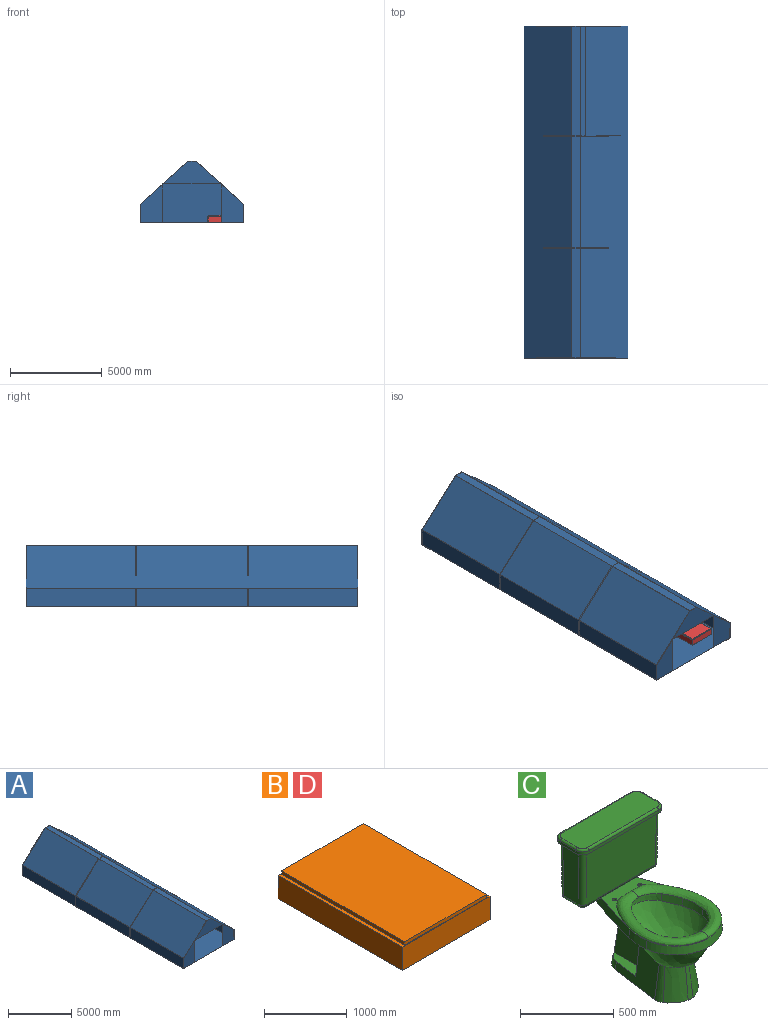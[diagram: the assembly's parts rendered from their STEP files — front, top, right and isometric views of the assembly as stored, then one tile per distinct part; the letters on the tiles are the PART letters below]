
ASSEMBLY  parts=4 mates=3
PART A: 45 faces, bbox 5640x18040x3323 mm
  f0: plane 5938.33x2228.5mm, normal (-0.67,0,-0.74), area 17807532.8mm2, adj f14,f26,f30,f36
  f1: plane 5963.33x2228.5mm, normal (0,0,1), area 13258575.8mm2, adj f14,f24,f26,f27,f30,f36
  f2: plane 3321.5x3313mm, normal (0,1,0), area 7985728.2mm2, adj f11,f12,f13,f15,f16,f35
  f3: plane 2093x25mm, normal (0,0,-1), area 52325mm2, adj f4,f24,f29,f35
  f4: plane 3321.5x3313mm, normal (0,-1,0), area 3600893.2mm2, adj f3,f11,f12,f13,f15,f16,f29,f35
  f5: plane 5938.33x994mm, normal (1,0,0), area 5902703.3mm2, adj f6,f9,f25,f34
  f6: plane 5938.33x2575.51mm, normal (0.67,0,-0.74), area 20580429.1mm2, adj f5,f10,f25,f34
  f7: plane 5938.33x2575.51mm, normal (-0.67,0,-0.74), area 20580429.1mm2, adj f8,f10,f25,f34
  f8: plane 5938.33x994mm, normal (-1,0,0), area 5902703.3mm2, adj f7,f9,f25,f34
  f9: plane 5963.33x5630mm, normal (0,0,1), area 33512141.7mm2, adj f5,f8,f23,f25,f31,f32,f34
  f10: plane 5938.33x478.98mm, normal (0,0,-1), area 2844337.9mm2, adj f6,f7,f25,f34
  f11: plane 5938.33x994mm, normal (1,0,0), area 5902703.3mm2, adj f2,f4,f12,f15
  f12: plane 5938.33x2575.51mm, normal (0.67,0,-0.74), area 20580429.1mm2, adj f2,f4,f11,f16
  f13: plane 5938.33x267.01mm, normal (-0.67,0,-0.74), area 2133631.1mm2, adj f2,f4,f16,f35
  f14: plane 5938.33x994mm, normal (-1,0,0), area 5902703.3mm2, adj f0,f1,f26,f30
  f15: plane 5963.33x3321.5mm, normal (0,0,1), area 19776499.2mm2, adj f2,f4,f11,f24,f29,f35
  f16: plane 5938.33x478.98mm, normal (0,0,-1), area 2844337.9mm2, adj f2,f4,f12,f13
  f17: plane 18040x1001.23mm, normal (1,0,0), area 18062119.6mm2, adj f18,f22,f23,f24
  f18: plane 18040x2578.59mm, normal (0.67,0,0.74), area 62595852mm2, adj f17,f19,f23,f24
  f19: plane 18040x482.82mm, normal (0,0,1), area 8710033mm2, adj f18,f20,f23,f24
  f20: plane 18040x2578.59mm, normal (-0.67,0,0.74), area 62595852mm2, adj f19,f21,f23,f24
  f21: plane 18040x1001.23mm, normal (-1,0,0), area 18062119.6mm2, adj f20,f22,f23,f24
  f22: plane 18040x5640mm, normal (0,0,-1), area 101745600mm2, adj f17,f21,f23,f24
  f23: plane 5640x3323mm, normal (0,-1,0), area 6107379.6mm2, adj f9,f17,f18,f19,f20,f21,f22,f31
  f24: plane 5640x3323mm, normal (0,1,0), area 6274979.6mm2, adj f1,f3,f15,f17,f18,f19,f20,f21
  f25: plane 5630x3313mm, normal (0,-1,0), area 12679581.3mm2, adj f5,f6,f7,f8,f9,f10
  f26: plane 3000.55x2228.5mm, normal (0,1,0), area 4450927.8mm2, adj f0,f1,f14,f36
  f27: plane 2095x25mm, normal (-1,0,0), area 52375mm2, adj f1,f24,f28,f30
  f28: plane 1000x25mm, normal (0,0,-1), area 25000mm2, adj f24,f27,f30,f36
  f29: plane 2095x25mm, normal (1,0,0), area 52375mm2, adj f3,f4,f15,f24
  f30: plane 3000.55x2228.5mm, normal (0,-1,0), area 2355927.8mm2, adj f0,f1,f14,f27,f28,f36
  f31: plane 2095x25mm, normal (-1,0,0), area 52375mm2, adj f9,f23,f33,f34
  f32: plane 2095x25mm, normal (1,0,0), area 52375mm2, adj f9,f23,f33,f34
  f33: plane 3173x25mm, normal (0,0,-1), area 79325mm2, adj f23,f31,f32,f34
  f34: plane 5630x3313mm, normal (0,1,0), area 6032146.3mm2, adj f5,f6,f7,f8,f9,f10,f31,f32
  f35: plane 5963.33x3072.58mm, normal (-1,0,0), area 18298395.5mm2, adj f2,f3,f4,f13,f15,f24
  f36: plane 5963.33x3000.55mm, normal (1,0,0), area 17870643.5mm2, adj f0,f1,f24,f26,f28,f30
  f37: plane 5630x3313mm, normal (0,-1,0), area 12679581.3mm2, adj f39,f40,f41,f42,f43,f44
  f38: plane 5630x3313mm, normal (0,1,0), area 12679581.3mm2, adj f39,f40,f41,f42,f43,f44
  f39: plane 6013.33x5630mm, normal (0,0,1), area 33855066.7mm2, adj f37,f38,f40,f43
  f40: plane 6013.33x994mm, normal (-1,0,0), area 5977253.3mm2, adj f37,f38,f39,f41
  f41: plane 6013.33x2575.51mm, normal (-0.67,0,-0.74), area 20840355.9mm2, adj f37,f38,f40,f44
  f42: plane 6013.33x2575.51mm, normal (0.67,0,-0.74), area 20840355.9mm2, adj f37,f38,f43,f44
  f43: plane 6013.33x994mm, normal (1,0,0), area 5977253.3mm2, adj f37,f38,f39,f42
  f44: plane 6013.33x478.98mm, normal (0,0,-1), area 2880261.3mm2, adj f37,f38,f41,f42
PART B: 16 faces, bbox 1500x2120x395 mm
  f0: plane 2120x1500mm, normal (0,0,1), area 240000mm2, adj f1,f2,f3,f4,f5,f6,f7,f8
  f1: plane 2120x345mm, normal (-1,0,0), area 731400mm2, adj f0,f2,f4,f14
  f2: plane 1500x345mm, normal (0,-1,0), area 517500mm2, adj f0,f1,f3,f14
  f3: plane 2120x345mm, normal (1,0,0), area 731400mm2, adj f0,f2,f4,f14
  f4: plane 1500x345mm, normal (0,1,0), area 517500mm2, adj f0,f1,f3,f14
  f5: plane 2100x50mm, normal (-1,0,0), area 105000mm2, adj f0,f6,f8,f9
  f6: plane 1400x50mm, normal (0,-1,0), area 70000mm2, adj f0,f5,f7,f9
  f7: plane 2100x50mm, normal (1,0,0), area 105000mm2, adj f0,f6,f8,f9
  f8: plane 1400x50mm, normal (0,1,0), area 70000mm2, adj f0,f5,f7,f9
  f9: plane 2100x1400mm, normal (0,0,1), area 2940000mm2, adj f5,f6,f7,f8
  f10: plane 1450x320mm, normal (0,-1,0), area 464000mm2, adj f11,f13,f14,f15
  f11: plane 2070x320mm, normal (1,0,0), area 662400mm2, adj f10,f12,f14,f15
  f12: plane 1450x320mm, normal (0,1,0), area 464000mm2, adj f11,f13,f14,f15
  f13: plane 2070x320mm, normal (-1,0,0), area 662400mm2, adj f10,f12,f14,f15
  f14: plane 2120x1500mm, normal (0,0,-1), area 178500mm2, adj f1,f2,f3,f4,f10,f11,f12,f13
  f15: plane 2070x1450mm, normal (0,0,-1), area 3001500mm2, adj f10,f11,f12,f13
PART C: 178 faces, bbox 660.3x888.4x889 mm
  f0: plane 6.63x6.46mm, normal (0,0,-1), area 25mm2, adj f11,f12,f13,f110
  f1: plane 6.43x3.66mm, normal (0,0,-1), area 12.9mm2, adj f18,f108,f109
  f2: plane 6.63x6.46mm, normal (0,0,-1), area 25mm2, adj f28,f29,f30,f110
  f3: plane 6.43x3.66mm, normal (0,0,-1), area 12.9mm2, adj f35,f111,f112
  f4: plane 589.56x500.14mm, normal (0,0,-1), area 105064.3mm2, adj f5,f6,f7,f8,f9,f14,f15,f16
  f5: bspline ~589.56x250.07mm, area 66336.6mm2, adj f4,f22
  f6: plane 29.24x25.8mm, normal (0.66,-0.75,0), area 117mm2, adj f4,f7,f9,f11
  f7: cylinder r=7.5mm len=13.12mm, axis (0,0,1), area 70.7mm2, adj f4,f6,f8,f13
  f8: plane 29.24x25.8mm, normal (-0.66,0.75,0), area 117mm2, adj f4,f7,f9,f12
  f9: cylinder r=7.5mm len=13.12mm, axis (0,0,1), area 70.7mm2, adj f4,f6,f8,f10
  f10: torus R=3.5mm, axis (0,0,1), area 119.4mm2, adj f9,f11,f12,f39
  f11: cylinder r=4mm len=31.89mm, axis (0.75,0.66,0), area 245mm2, adj f0,f6,f10,f13,f39
  f12: cylinder r=4mm len=31.89mm, axis (-0.75,-0.66,0), area 245mm2, adj f0,f8,f10,f13,f39
  f13: torus R=3.5mm, axis (0,0,1), area 119.4mm2, adj f0,f7,f11,f12
  f14: cylinder r=7.5mm len=14.64mm, axis (0,0,1), area 70.7mm2, adj f4,f15,f17,f21
  f15: plane 37.1x12.02mm, normal (0.31,0.95,0), area 117mm2, adj f4,f14,f16,f20
  f16: cylinder r=7.5mm len=14.64mm, axis (0,0,1), area 70.7mm2, adj f4,f15,f17,f18
  f17: plane 37.1x12.02mm, normal (-0.31,-0.95,0), area 117mm2, adj f4,f14,f16,f19
  f18: torus R=3.5mm, axis (0,0,1), area 119.4mm2, adj f1,f16,f19,f20,f39
  f19: cylinder r=4mm len=38.34mm, axis (0.95,-0.31,0), area 245mm2, adj f17,f18,f21,f39
  f20: cylinder r=4mm len=38.34mm, axis (-0.95,0.31,0), area 245mm2, adj f15,f18,f21,f39
  f21: torus R=3.5mm, axis (0,0,1), area 119.4mm2, adj f14,f19,f20,f39
  f22: bspline ~589.56x250.07mm, area 66336.6mm2, adj f4,f5
  f23: plane 29.24x25.8mm, normal (-0.66,-0.75,0), area 117mm2, adj f4,f24,f26,f28
  f24: cylinder r=7.5mm len=13.12mm, axis (0,0,1), area 70.7mm2, adj f4,f23,f25,f30
  f25: plane 29.24x25.8mm, normal (0.66,0.75,0), area 117mm2, adj f4,f24,f26,f29
  f26: cylinder r=7.5mm len=13.12mm, axis (0,0,1), area 70.7mm2, adj f4,f23,f25,f27
  f27: torus R=3.5mm, axis (0,0,1), area 119.4mm2, adj f26,f28,f29,f39
  f28: cylinder r=4mm len=31.89mm, axis (-0.75,0.66,0), area 245mm2, adj f2,f23,f27,f30,f39
  f29: cylinder r=4mm len=31.89mm, axis (0.75,-0.66,0), area 245mm2, adj f2,f25,f27,f30,f39
  f30: torus R=3.5mm, axis (0,0,1), area 119.4mm2, adj f2,f24,f28,f29
  f31: cylinder r=7.5mm len=14.64mm, axis (0,0,1), area 70.7mm2, adj f4,f32,f34,f38
  f32: plane 37.1x12.02mm, normal (-0.31,0.95,0), area 117mm2, adj f4,f31,f33,f37
  f33: cylinder r=7.5mm len=14.64mm, axis (0,0,1), area 70.7mm2, adj f4,f32,f34,f35
  f34: plane 37.1x12.02mm, normal (0.31,-0.95,0), area 117mm2, adj f4,f31,f33,f36
  f35: torus R=3.5mm, axis (0,0,1), area 119.4mm2, adj f3,f33,f36,f37,f39
  f36: cylinder r=4mm len=38.34mm, axis (-0.95,-0.31,0), area 245mm2, adj f34,f35,f38,f39
  f37: cylinder r=4mm len=38.34mm, axis (0.95,0.31,0), area 245mm2, adj f32,f35,f38,f39
  f38: torus R=3.5mm, axis (0,0,1), area 119.4mm2, adj f31,f36,f37,f39
  f39: plane 682.07x486.65mm, normal (0,0,1), area 110534.9mm2, adj f10,f11,f12,f18,f19,f20,f21,f27
  f40: plane 601.26x191.84mm, normal (0,0,-1), area 7653mm2, adj f50,f51,f52,f53,f54,f55,f56,f57
  f41: cylinder r=49.83mm len=49.83mm, axis (0,0,1), area 1491.1mm2, adj f42,f48,f49,f65
  f42: plane 117.58x19.05mm, normal (-1,0,0), area 2239.9mm2, adj f41,f43,f49,f66
  f43: cylinder r=49.83mm len=49.83mm, axis (0,0,1), area 1491.1mm2, adj f42,f44,f49,f64
  f44: plane 527x19.05mm, normal (0,1,0), area 10039.4mm2, adj f43,f45,f49,f62
  f45: cylinder r=49.83mm len=49.83mm, axis (0,0,1), area 1491.1mm2, adj f44,f46,f49,f60
  f46: plane 117.58x19.05mm, normal (1,0,0), area 2239.9mm2, adj f45,f47,f49,f59
  f47: cylinder r=49.83mm len=49.83mm, axis (0,0,1), area 1491.1mm2, adj f46,f48,f49,f61
  f48: plane 527x19.05mm, normal (0,-1,0), area 10039.4mm2, adj f41,f47,f49,f63
  f49: plane 626.66x217.24mm, normal (0,0,-1), area 19842mm2, adj f41,f42,f43,f44,f45,f46,f47,f48
  f50: cylinder r=37.13mm len=37.13mm, axis (0,0,1), area 370.4mm2, adj f40,f49,f51,f57
  f51: plane 117.58x6.35mm, normal (-1,0,0), area 746.6mm2, adj f40,f49,f50,f52
  f52: cylinder r=37.13mm len=37.13mm, axis (0,0,1), area 370.4mm2, adj f40,f49,f51,f53
  f53: plane 527x6.35mm, normal (0,1,0), area 3346.5mm2, adj f40,f49,f52,f54
  f54: cylinder r=37.13mm len=37.13mm, axis (0,0,1), area 370.4mm2, adj f40,f49,f53,f55
  f55: plane 117.58x6.35mm, normal (1,0,0), area 746.6mm2, adj f40,f49,f54,f56
  f56: cylinder r=37.13mm len=37.13mm, axis (0,0,1), area 370.4mm2, adj f40,f49,f55,f57
  f57: plane 527x6.35mm, normal (0,-1,0), area 3346.5mm2, adj f40,f49,f50,f56
  f58: plane 601.26x191.84mm, normal (0,0,1), area 114163.7mm2, adj f59,f60,f61,f62,f63,f64,f65,f66
  f59: cylinder r=12.7mm len=117.58mm, axis (0,-1,0), area 2345.6mm2, adj f46,f58,f60,f61
  f60: torus R=37.13mm, axis (0,0,1), area 1416.9mm2, adj f45,f58,f59,f62
  f61: torus R=37.13mm, axis (0,0,1), area 1416.9mm2, adj f47,f58,f59,f63
  f62: cylinder r=12.7mm len=527mm, axis (1,0,0), area 10513.2mm2, adj f44,f58,f60,f64
  f63: cylinder r=12.7mm len=527mm, axis (-1,0,0), area 10513.2mm2, adj f48,f58,f61,f65
  f64: torus R=37.13mm, axis (0,0,1), area 1416.9mm2, adj f43,f58,f62,f66
  f65: torus R=37.13mm, axis (0,0,1), area 1416.9mm2, adj f41,f58,f63,f66
  f66: cylinder r=12.7mm len=117.58mm, axis (0,1,0), area 2345.6mm2, adj f42,f58,f64,f65
  f67: plane 26.5x26.5mm, normal (0,0,-1), area 551.7mm2, adj f69
  f68: plane 26.5x26.5mm, normal (0,0,-1), area 551.7mm2, adj f70
  f69: cylinder r=13.25mm len=31.7mm, axis (0,0,1), area 1450.3mm2, adj f67,f102,f103,f127
  f70: cylinder r=13.25mm len=31.7mm, axis (0,0,1), area 1450.6mm2, adj f68,f105,f106,f127
  f71: cylinder r=11.96mm len=23.92mm, axis (0,0,1), area 954.4mm2, adj f39,f127
  f72: cylinder r=11.96mm len=23.92mm, axis (0,0,1), area 954.4mm2, adj f39,f127
  f73: plane 203.2x38.1mm, normal (0.71,0.71,0), area 10948.7mm2, adj f74,f75,f76,f77
  f74: plane 237.76x74.36mm, normal (0,0,1), area 12302.8mm2, adj f73,f76,f77,f131,f132
  f75: plane 204.52x45.54mm, normal (0,0,-1), area 5536.8mm2, adj f73,f76,f77,f131,f132
  f76: plane 203.2x36.26mm, normal (0,1,0), area 4439.1mm2, adj f73,f74,f75,f131
  f77: plane 207.01x203.47mm, normal (1,0,0), area 37269.3mm2, adj f73,f74,f75,f132
  f78: plane 203.2x38.1mm, normal (-0.71,0.71,0), area 10948.7mm2, adj f79,f80,f81,f82
  f79: plane 237.76x74.36mm, normal (0,0,1), area 12302.8mm2, adj f78,f81,f82,f130,f132
  f80: plane 204.52x45.54mm, normal (0,0,-1), area 5536.8mm2, adj f78,f81,f82,f130,f132
  f81: plane 207.01x203.47mm, normal (-1,0,0), area 37269.3mm2, adj f78,f79,f80,f132
  f82: plane 203.2x36.26mm, normal (0,1,0), area 4439.1mm2, adj f78,f79,f80,f130
  f83: plane 560.3x287.95mm, normal (0,0,-1), area 123539mm2, adj f84,f85,f86,f87,f88,f130,f131,f132
  f84: cone r=76.2mm half-angle=8deg, axis (0,0,-1), area 10378.2mm2, adj f83,f85,f126,f131
  f85: cone r=197.74mm half-angle=8deg, axis (0,0,-1), area 27185.8mm2, adj f83,f84,f86,f126
  f86: cone r=76.2mm half-angle=8deg, axis (0,0,-1), area 6573mm2, adj f83,f85,f87,f126
  f87: cone r=197.74mm half-angle=8deg, axis (0,0,-1), area 27152.3mm2, adj f83,f86,f88,f126
  f88: cone r=76.2mm half-angle=8deg, axis (0,0,-1), area 10372.1mm2, adj f83,f87,f126,f130
  f89: offset ~583.11x463.72mm, area 264467.6mm2, adj f90,f91,f92,f93,f94,f95
  f90: cylinder r=337.73mm len=141.19mm, axis (0,0,1), area 601mm2, adj f89,f91,f95,f114
  f91: cylinder r=970.9mm len=115.37mm, axis (0,0,1), area 405.1mm2, adj f89,f90,f92,f114
  f92: cylinder r=148.33mm len=268.25mm, axis (0,0,1), area 940.7mm2, adj f89,f91,f93,f114
  f93: cylinder r=970.9mm len=115.37mm, axis (0,0,1), area 397.7mm2, adj f89,f92,f94,f114
  f94: cylinder r=337.73mm len=141.19mm, axis (0,0,1), area 570.6mm2, adj f89,f93,f95,f114
  f95: cylinder r=195.4mm len=388.44mm, axis (0,0,1), area 2589.6mm2, adj f89,f90,f94,f114
  f96: cylinder r=208.1mm len=413.69mm, axis (0,0,1), area 3860.1mm2, adj f97,f100,f123,f126
  f97: cylinder r=350.43mm len=146.5mm, axis (0,0,1), area 942.1mm2, adj f96,f98,f123,f126
  f98: cylinder r=983.6mm len=116.88mm, axis (0,0,1), area 798.9mm2, adj f97,f123,f125,f126
  f99: cylinder r=983.6mm len=116.88mm, axis (0,0,1), area 798.9mm2, adj f100,f123,f124,f126
  f100: cylinder r=350.43mm len=146.5mm, axis (0,0,1), area 942.2mm2, adj f96,f99,f123,f126
  f101: plane 38.43x32.77mm, normal (0,0.93,-0.36), area 737mm2, adj f102,f123,f127,f129
  f102: cone r=3586.69mm half-angle=21deg, axis (0,0,-1), area 10140.2mm2, adj f69,f101,f103,f123,f127
  f103: cone r=88.16mm half-angle=21deg, axis (0,0,-1), area 3307.5mm2, adj f69,f102,f104,f123,f127
  f104: cone r=218.65mm half-angle=21deg, axis (0,0,-1), area 1626.9mm2, adj f103,f105,f123,f127
  f105: cone r=88.16mm half-angle=21deg, axis (0,0,-1), area 3307.9mm2, adj f70,f104,f106,f123,f127
  f106: cone r=3586.69mm half-angle=21deg, axis (0,0,-1), area 10140.2mm2, adj f70,f105,f107,f123,f127
  f107: plane 38.43x32.77mm, normal (0,0.93,-0.36), area 737mm2, adj f106,f123,f127,f128
  f108: cone r=967.16mm half-angle=10deg, axis (0,0,1), area 6351.6mm2, adj f1,f39,f109,f113,f114
  f109: cone r=333.99mm half-angle=10deg, axis (0,0,1), area 7196.3mm2, adj f1,f39,f108,f110,f114
  f110: cone r=191.66mm half-angle=10deg, axis (0,0,1), area 28206.9mm2, adj f0,f2,f39,f109,f111,f114
  f111: cone r=333.99mm half-angle=10deg, axis (0,0,1), area 7196.3mm2, adj f3,f39,f110,f112,f114
  f112: cone r=967.16mm half-angle=10deg, axis (0,0,1), area 6351.6mm2, adj f3,f39,f111,f113,f114
  f113: cone r=144.58mm half-angle=10deg, axis (0,0,1), area 16328.2mm2, adj f39,f108,f112,f114
  f114: plane 515.49x392.53mm, normal (0,0,-1), area 17785mm2, adj f90,f91,f92,f93,f94,f95,f108,f109
  f115: cone r=235.09mm half-angle=10deg, axis (0,0,-1), area 2331.5mm2, adj f116,f122,f123,f135
  f116: cone r=104.6mm half-angle=10deg, axis (0,0,-1), area 6259.1mm2, adj f115,f117,f123,f135,f150
  f117: cone r=3603.13mm half-angle=10deg, axis (0,0,-1), area 20573.2mm2, adj f39,f116,f118,f123,f150
  f118: cone r=384.79mm half-angle=10deg, axis (0,0,-1), area 7301.9mm2, adj f39,f117,f119,f123
  f119: cone r=242.46mm half-angle=10deg, axis (0,0,-1), area 37211.9mm2, adj f39,f118,f120,f123
  f120: cone r=384.79mm half-angle=10deg, axis (0,0,-1), area 7301.9mm2, adj f39,f119,f121,f123
  f121: cone r=3603.13mm half-angle=10deg, axis (0,0,-1), area 20573.2mm2, adj f39,f120,f122,f123,f141
  f122: cone r=104.6mm half-angle=10deg, axis (0,0,-1), area 6259.2mm2, adj f115,f121,f123,f135,f141
  f123: plane 819.76x504.56mm, normal (0,0,-1), area 74259.2mm2, adj f96,f97,f98,f99,f100,f101,f102,f103
  f124: cylinder r=161.03mm len=102.27mm, axis (0,0,1), area 873.4mm2, adj f99,f126,f128,f131
  f125: cylinder r=161.03mm len=102.27mm, axis (0,0,1), area 873.4mm2, adj f98,f126,f129,f130
  f126: bspline ~557.71x438.33mm, area 217099mm2, adj f84,f85,f86,f87,f88,f96,f97,f98
  f127: plane 316.67x273.18mm, normal (0,0,-1), area 36562.5mm2, adj f69,f70,f71,f72,f101,f102,f103,f104
  f128: cone r=161.03mm half-angle=21deg, axis (0,0,1), area 5939.9mm2, adj f107,f124,f127,f131
  f129: cone r=161.03mm half-angle=21deg, axis (0,0,1), area 5939.9mm2, adj f101,f125,f127,f130
  f130: plane 445.06x347.95mm, normal (-0.98,0.13,0.14), area 70082.7mm2, adj f79,f80,f82,f83,f88,f125,f126,f127
  f131: plane 445.06x348.01mm, normal (0.98,0.13,0.14), area 69662.7mm2, adj f74,f75,f76,f83,f84,f124,f126,f127
  f132: cone r=97.69mm half-angle=8deg, axis (0,0,-1), area 57658.1mm2, adj f74,f75,f77,f79,f80,f81,f83,f127
  f133: torus R=0.44mm, axis (0,0,1), area 1023mm2, adj f134,f135,f145,f150
  f134: cylinder r=25.4mm len=117.58mm, axis (0,1,0), area 4639.1mm2, adj f133,f136,f144,f150
  f135: cylinder r=25.4mm len=527mm, axis (1,0,0), area 20749.3mm2, adj f115,f116,f122,f133,f137,f141,f146,f150
  f136: torus R=0.44mm, axis (0,0,1), area 1023mm2, adj f134,f138,f143,f150
  f137: torus R=0.44mm, axis (0,0,1), area 1023mm2, adj f135,f139,f141,f147
  f138: cylinder r=25.4mm len=527mm, axis (-1,0,0), area 20792.8mm2, adj f39,f136,f140,f141,f142,f150
  f139: cylinder r=25.4mm len=117.58mm, axis (0,-1,0), area 4639.1mm2, adj f137,f140,f141,f148
  f140: torus R=0.44mm, axis (0,0,1), area 1023mm2, adj f138,f139,f141,f149
  f141: plane 239.27x118.47mm, normal (0,0,-1), area 19463.9mm2, adj f121,f122,f135,f137,f138,f139,f140
  f142: plane 527x356.04mm, normal (0,-1,-0.02), area 187664.1mm2, adj f40,f138,f143,f149
  f143: cone r=25.4mm half-angle=1deg, axis (0,0,1), area 16189.5mm2, adj f40,f136,f142,f144
  f144: plane 356.04x117.58mm, normal (-1,0,-0.02), area 41870.2mm2, adj f40,f134,f143,f145
  f145: cone r=25.4mm half-angle=1deg, axis (0,0,1), area 16189.5mm2, adj f40,f133,f144,f146
  f146: plane 527x356.04mm, normal (0,1,-0.02), area 187664.1mm2, adj f40,f135,f145,f147
  f147: cone r=25.4mm half-angle=1deg, axis (0,0,1), area 16189.5mm2, adj f40,f137,f146,f148
  f148: plane 356.04x117.58mm, normal (1,0,-0.02), area 41870.2mm2, adj f40,f139,f147,f149
  f149: cone r=25.4mm half-angle=1deg, axis (0,0,1), area 16189.5mm2, adj f40,f140,f142,f148
  f150: plane 239.27x118.47mm, normal (0,0,-1), area 19464mm2, adj f116,f117,f133,f134,f135,f136,f138
  f151: plane 588.56x179.14mm, normal (0,0,-1), area 104622.7mm2, adj f152,f153,f154,f155,f156,f157,f158,f159
  f152: plane 527x12.7mm, normal (0,-1,0), area 6692.9mm2, adj f151,f153,f159,f160
  f153: cylinder r=30.78mm len=30.78mm, axis (0,0,-1), area 614mm2, adj f151,f152,f154,f160
  f154: plane 117.58x12.7mm, normal (1,0,0), area 1493.3mm2, adj f151,f153,f155,f160
  f155: cylinder r=30.78mm len=30.78mm, axis (0,0,-1), area 614mm2, adj f151,f154,f156,f160
  f156: plane 527x12.7mm, normal (0,1,0), area 6692.9mm2, adj f151,f155,f157,f160
  f157: cylinder r=30.78mm len=30.78mm, axis (0,0,-1), area 614mm2, adj f151,f156,f158,f160
  f158: plane 117.58x12.7mm, normal (-1,0,0), area 1493.3mm2, adj f151,f157,f159,f160
  f159: cylinder r=30.78mm len=30.78mm, axis (0,0,-1), area 614mm2, adj f151,f152,f158,f160
  f160: plane 588.56x179.14mm, normal (0,0,1), area 16538mm2, adj f152,f153,f154,f155,f156,f157,f158,f159
  f161: cone r=12.7mm half-angle=1deg, axis (0,0,1), area 9080mm2, adj f160,f162,f168,f170
  f162: plane 355.82x117.58mm, normal (-1,0,0.02), area 41844.2mm2, adj f160,f161,f163,f171
  f163: cone r=12.7mm half-angle=1deg, axis (0,0,1), area 9080mm2, adj f160,f162,f164,f173
  f164: plane 527x355.82mm, normal (0,-1,0.02), area 187547.2mm2, adj f160,f163,f165,f175
  f165: cone r=12.7mm half-angle=1deg, axis (0,0,1), area 9080mm2, adj f160,f164,f166,f177
  f166: plane 355.82x117.58mm, normal (1,0,0.02), area 41844.2mm2, adj f160,f165,f167,f176
  f167: cone r=12.7mm half-angle=1deg, axis (0,0,1), area 9080mm2, adj f160,f166,f168,f174
  f168: plane 527x355.82mm, normal (0,1,0.02), area 187547.2mm2, adj f160,f161,f167,f172
  f169: plane 527.88x118.46mm, normal (0,0,1), area 62532.5mm2, adj f170,f171,f172,f173,f174,f175,f176,f177
  f170: torus R=0.44mm, axis (0,0,1), area 262.6mm2, adj f161,f169,f171,f172
  f171: cylinder r=12.7mm len=117.58mm, axis (0,-1,0), area 2319.6mm2, adj f162,f169,f170,f173
  f172: cylinder r=12.7mm len=527mm, axis (-1,0,0), area 10396.4mm2, adj f168,f169,f170,f174
  f173: torus R=0.44mm, axis (0,0,1), area 262.6mm2, adj f163,f169,f171,f175
  f174: torus R=0.44mm, axis (0,0,1), area 262.6mm2, adj f167,f169,f172,f176
  f175: cylinder r=12.7mm len=527mm, axis (1,0,0), area 10396.4mm2, adj f164,f169,f173,f177
  f176: cylinder r=12.7mm len=117.58mm, axis (0,1,0), area 2319.6mm2, adj f166,f169,f174,f177
  f177: torus R=0.44mm, axis (0,0,1), area 262.6mm2, adj f165,f169,f175,f176
PART D: same geometry as B
PLACE A t=(-4567.97,4910.05,2121)mm
PLACE B t=(-3514.02,2090.25,2441)mm
PLACE C rot(axis=(0,0,1),90deg) t=(-3384.42,853.43,2578.2)mm
PLACE D t=(-896.45,-12221.91,2441)mm
MATE planar C.f83 <-> A.f15  axis (0,0,-1) through (-3552.32,853.43,2121)mm
MATE planar D.f14 <-> A.f9  axis (0,0,-1) through (-146.45,-10092.71,2121)mm
MATE planar B.f14 <-> A.f15  axis (0,0,-1) through (-2764.02,3184.44,2121)mm
